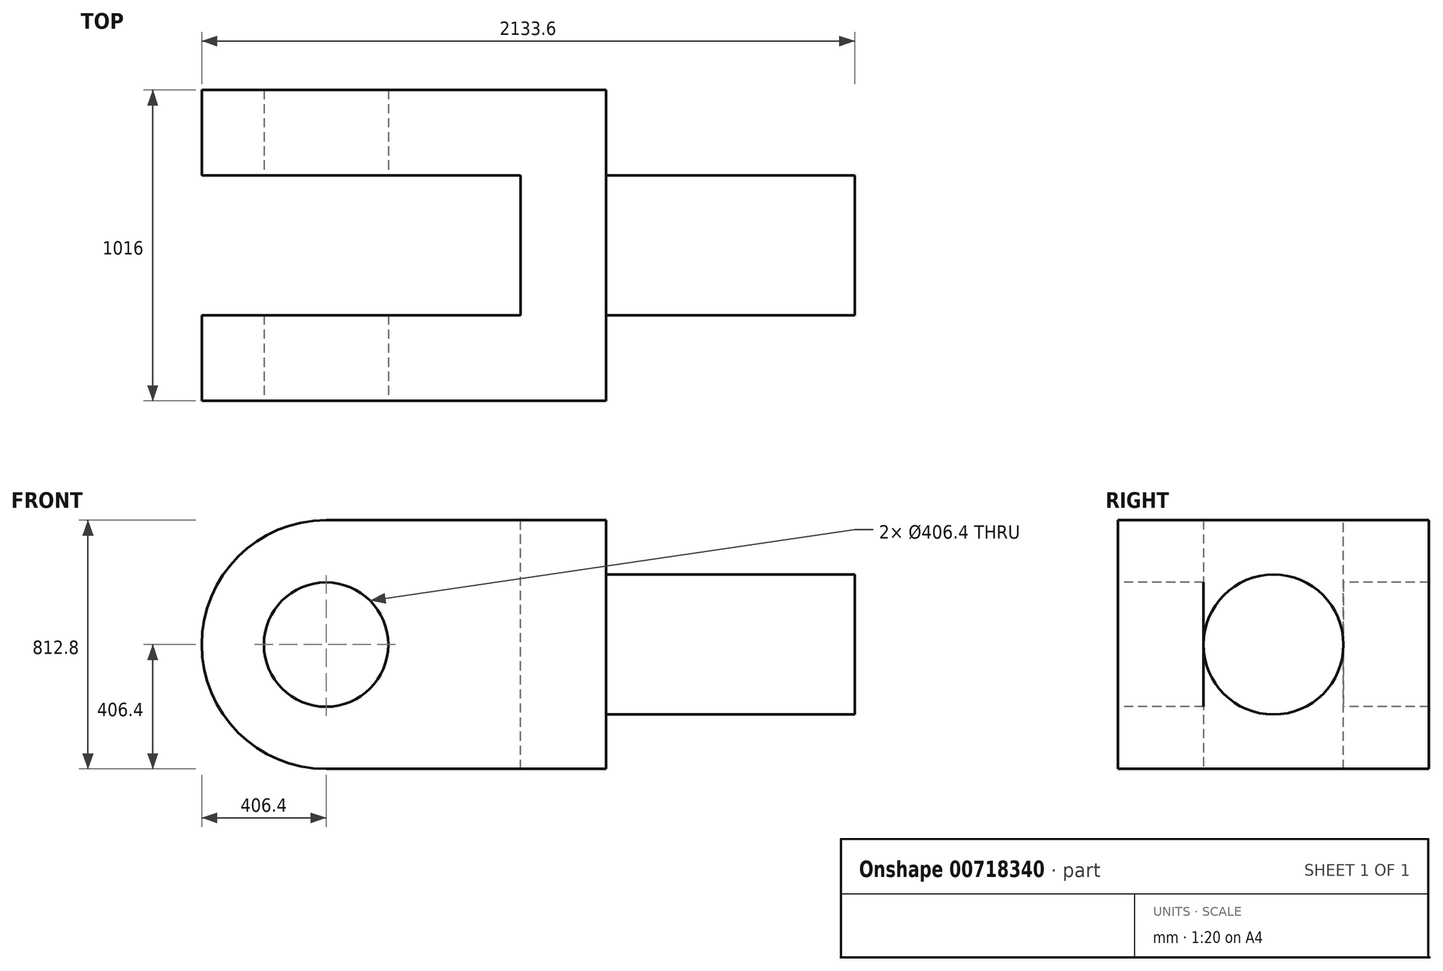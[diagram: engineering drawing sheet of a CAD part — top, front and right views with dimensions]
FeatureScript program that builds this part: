
annotation { "Feature Type Name" : "Feature", "Feature Type Description" : "" }
export const myFeature = defineFeature(function(context is Context, id is Id, definition is map)
    precondition{}
    {
        {
            var Q0;
            Q0=qCreatedBy(makeId("Top.planeOp"),FACE);
            var sketch = newSketch(context, id + "F0", { "sketchPlane" : qUnion([Q0])});
            skLineSegment(sketch, "E0", {"start": v(-115.6, 51.7) * mm, "end": v(1205.2, 51.7) * mm});
            skLineSegment(sketch, "E1", {"start": v(1205.2, 51.7) * mm, "end": v(1205.2, -964.3) * mm});
            skLineSegment(sketch, "E2", {"start": v(1205.2, -964.3) * mm, "end": v(-115.6, -964.3) * mm});
            skLineSegment(sketch, "E3", {"start": v(-115.6, -964.3) * mm, "end": v(-115.6, -684.9) * mm});
            skLineSegment(sketch, "E4", {"start": v(-115.6, -684.9) * mm, "end": v(925.8, -684.9) * mm});
            skLineSegment(sketch, "E5", {"start": v(925.8, -684.9) * mm, "end": v(925.8, -227.7) * mm});
            skLineSegment(sketch, "E6", {"start": v(925.8, -227.7) * mm, "end": v(-115.6, -227.7) * mm});
            skLineSegment(sketch, "E7", {"start": v(-115.6, -227.7) * mm, "end": v(-115.6, 51.7) * mm});
            skLineSegment(sketch, "E8", {"start": v(1205.2, 51.7) * mm, "end": v(1205.2, -227.7) * mm});
            skSolve(sketch);
        }
        {
            var Q0;
            Q0=qSketchRegion(id+"F0",true);
            extrude(context, id + "F1", {"entities" : qUnion([Q0]), "oppositeDirection" : true, "depth" : 812.8 * mm, "offsetDistance" : 25.4 * mm});
        }
        {
            var Q0;
            Q0=makeQuery(id+"F1.opExtrude","SWEPT_FACE",FACE,{"disambiguationData":[OSD([sQuery(id+"F0.wireOp",EDGE,"E2")])]});
            var sketch = newSketch(context, id + "F2", { "sketchPlane" : qUnion([Q0])});
            skLineSegment(sketch, "E9", {"start": v(1205.2, 0) * mm, "end": v(290.8, 0) * mm});
            skLineSegment(sketch, "E10", {"start": v(290.8, 0) * mm, "end": v(290.8, -406.4) * mm});
            skCircle(sketch, "E11", {"center": v(290.8, -406.4) * mm, "radius": 203.2 * mm});
            skSolve(sketch);
        }
        {
            var Q0;
            Q0=makeQuery(id+"F2.imprint","IMPRINT",FACE,{"disambiguationData":[TD([[makeQuery(id+"F2.imprint","IMPRINT",EDGE,{"derivedFrom":sQuery(id+"F2.wireOp",EDGE,"E11")}),1.0]])]});
            extrude(context, id + "F3", {"entities" : qUnion([Q0]), "operationType" : NewBodyOperationType.REMOVE, "endBound" : BoundingType.THROUGH_ALL, "oppositeDirection" : true, "depth" : 25.4 * mm, "offsetDistance" : 25.4 * mm});
        }
        {
            var Q0;
            Q0=makeQuery(id+"F1.opExtrude","CAP_EDGE",EDGE,{"disambiguationData":[OSD([sQuery(id+"F0.wireOp",EDGE,"E7")])],"isStart":true});
            var Q1;
            Q1=makeQuery(id+"F1.opExtrude","CAP_EDGE",EDGE,{"disambiguationData":[OSD([sQuery(id+"F0.wireOp",EDGE,"E3")])],"isStart":true});
            fillet(context, id + "F4", {"entities" : qUnion([Q0, Q1]), "radius" : 406.4 * mm, "tangentPropagation" : true, "allowEdgeOverflow" : false});
        }
        {
            var Q0;
            Q0=makeQuery(id+"F1.opExtrude","CAP_EDGE",EDGE,{"disambiguationData":[OSD([sQuery(id+"F0.wireOp",EDGE,"E7")])],"isStart":false});
            var Q1;
            Q1=makeQuery(id+"F1.opExtrude","CAP_EDGE",EDGE,{"disambiguationData":[OSD([sQuery(id+"F0.wireOp",EDGE,"E3")])],"isStart":false});
            fillet(context, id + "F5", {"entities" : qUnion([Q0, Q1]), "radius" : 406.4 * mm, "tangentPropagation" : true, "allowEdgeOverflow" : false});
        }
        {
            var Q0;
            Q0=makeQuery(id+"F1.opExtrude","SWEPT_FACE",FACE,{"disambiguationData":[OSD([sQuery(id+"F0.wireOp",EDGE,"E1"),sQuery(id+"F0.wireOp",EDGE,"E8")])]});
            var sketch = newSketch(context, id + "F6", { "sketchPlane" : qUnion([Q0])});
            skLineSegment(sketch, "E12", {"start": v(51.7, 0) * mm, "end": v(-456.3, 0) * mm});
            skLineSegment(sketch, "E13", {"start": v(-456.3, 0) * mm, "end": v(-456.3, -406.4) * mm});
            skCircle(sketch, "E14", {"center": v(-456.3, -406.4) * mm, "radius": 228.6 * mm});
            skSolve(sketch);
        }
        {
            var Q0;
            Q0=makeQuery(id+"F6.imprint","IMPRINT",FACE,{"disambiguationData":[TD([[makeQuery(id+"F6.imprint","IMPRINT",EDGE,{"derivedFrom":sQuery(id+"F6.wireOp",EDGE,"E14")}),1.0]])]});
            extrude(context, id + "F7", {"entities" : qUnion([Q0]), "operationType" : NewBodyOperationType.ADD, "depth" : 812.8 * mm, "offsetDistance" : 25.4 * mm});
        }
    });
